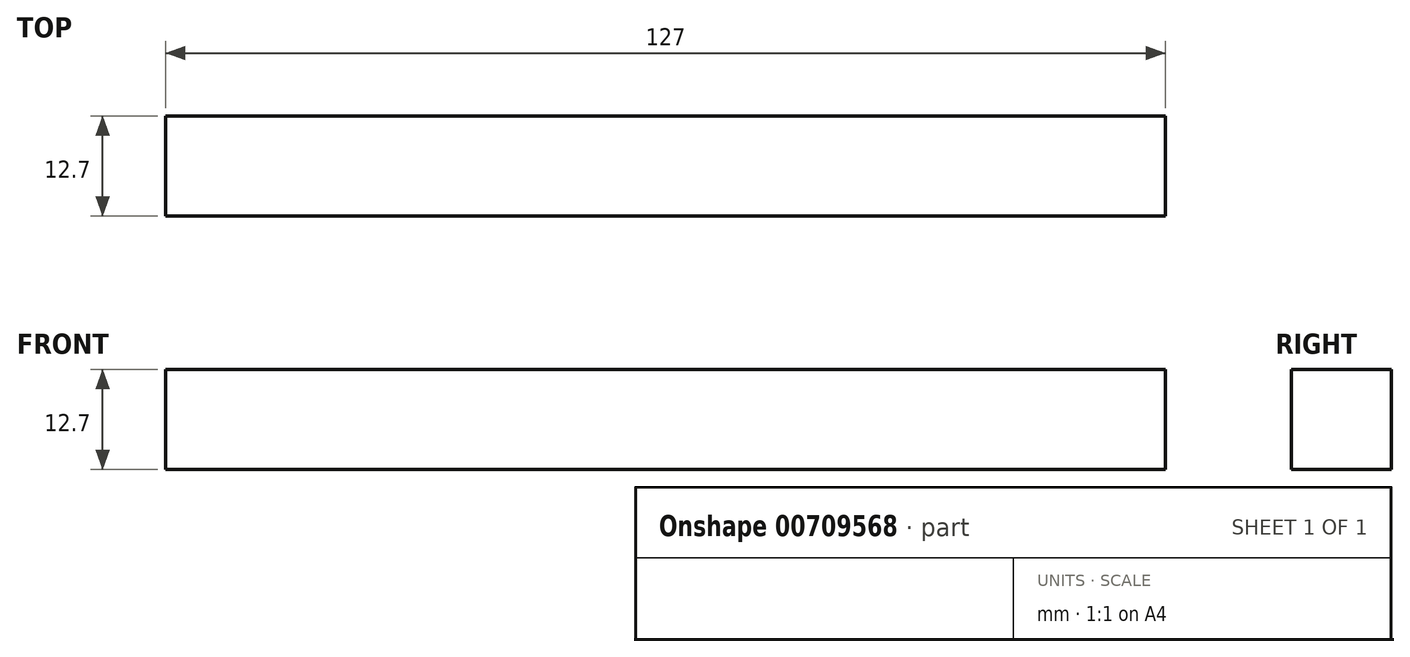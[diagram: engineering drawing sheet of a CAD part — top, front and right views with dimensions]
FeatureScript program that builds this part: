
annotation { "Feature Type Name" : "Feature", "Feature Type Description" : "" }
export const myFeature = defineFeature(function(context is Context, id is Id, definition is map)
    precondition{}
    {
        {
            var Q0;
            Q0=qCreatedBy(makeId("Front.planeOp"),FACE);
            var sketch = newSketch(context, id + "F0", { "sketchPlane" : qUnion([Q0])});
            skLineSegment(sketch, "E0.bottom", {"start": v(128.3, -2.76) * mm, "end": v(1.3, -2.76) * mm});
            skLineSegment(sketch, "E0.top", {"start": v(128.3, -15.46) * mm, "end": v(1.3, -15.46) * mm});
            skLineSegment(sketch, "E0.left", {"start": v(128.3, -2.76) * mm, "end": v(128.3, -15.46) * mm});
            skLineSegment(sketch, "E0.right", {"start": v(1.3, -2.76) * mm, "end": v(1.3, -15.46) * mm});
            skSolve(sketch);
        }
        {
            var Q0;
            Q0 = qSketchRegion(id + "F0", true);
            extrude(context, id + "F1", {"entities" : qUnion([Q0]), "depth" : 6.35 * mm, "offsetDistance" : 25.4 * mm, "hasSecondDirection" : true, "secondDirectionOppositeDirection" : true, "secondDirectionDepth" : 6.35 * mm});
        }
    });
